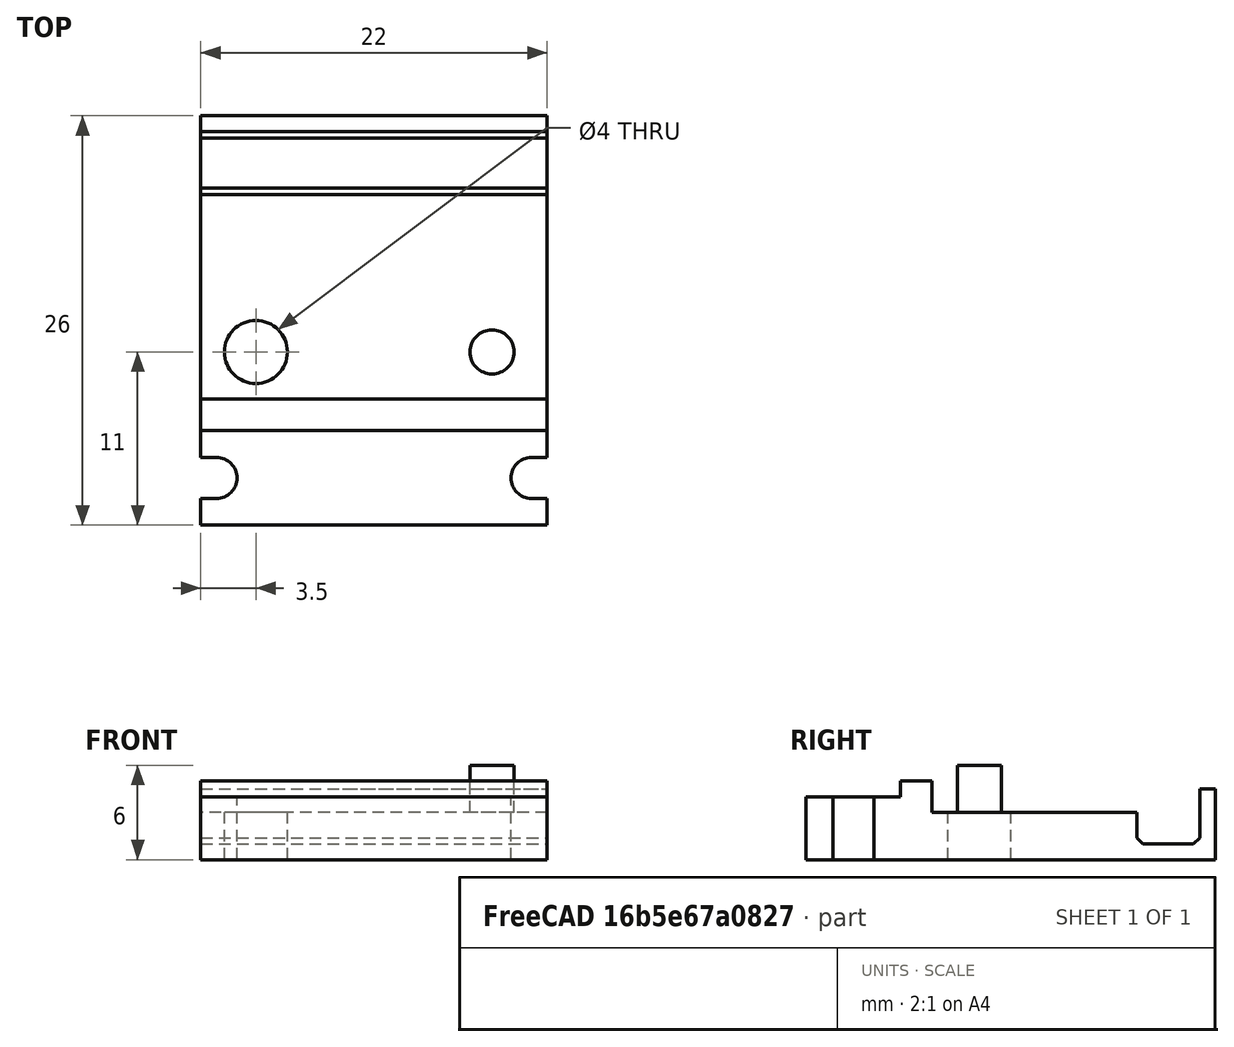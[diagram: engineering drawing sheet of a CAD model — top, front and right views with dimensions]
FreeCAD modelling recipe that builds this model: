
FCSTD DOCUMENT  (FreeCAD 0.18R16146 (Git))
Label: sensor-mount
License: All rights reserved
LicenseURL: http://en.wikipedia.org/wiki/All_rights_reserved
objects: Part::Box×4, Part::MultiFuse×4, Part::Cylinder×3, Part::Cut×3, Part::Feature×1
note: 15 computed .brp shape members not serialized (recipe doc carries the construction recipe); baked Part::Feature solids carry a one-line shape summary decoded from their .brp

FEATURE [Part::Feature] Chamfer002001  label="sensor-r002"
  Placement = pos=(0,0,3) rot=(0,0,1;0rad)
  shape: bbox 22 x 28 x 6 mm, 33 faces (baked)
FEATURE [Part::Cylinder] Cylinder
  Angle = 360
  AttacherType = Attacher::AttachEngine3D
  Height = 10
  Placement = pos=(-10,-5,0) rot=(0,0,1;0rad)
  Radius = 1.3
FEATURE [Part::Cylinder] Cylinder001
  Angle = 360
  AttacherType = Attacher::AttachEngine3D
  Height = 10
  Placement = pos=(10,-5,0) rot=(0,0,1;0rad)
  Radius = 1.3
FEATURE [Part::Box] Box001  label="Cube001"
  AttacherType = Attacher::AttachEngine3D
  Height = 10
  Length = 8
  Placement = pos=(10,-6.3,0) rot=(0,0,1;0rad)
  Width = 2.6
FEATURE [Part::Box] Box002  label="Cube002"
  AttacherType = Attacher::AttachEngine3D
  Height = 10
  Length = 8
  Placement = pos=(-18,-6.3,0) rot=(0,0,1;0rad)
  Width = 2.6
FEATURE [Part::Box] Box003  label="Cube003"
  AttacherType = Attacher::AttachEngine3D
  Height = 10
  Length = 10
  Placement = pos=(-12,18,0) rot=(0,0,1;0rad)
  Width = 10
FEATURE [Part::Cut] Cut
  Base = -> Chamfer002001
  Tool = -> Box003
FEATURE [Part::Box] Box  label="Cube"
  AttacherType = Attacher::AttachEngine3D
  Height = 4
  Length = 22
  Placement = pos=(-11,-8,0) rot=(0,0,1;0rad)
  Width = 6
FEATURE [Part::MultiFuse] Fusion001
  Shapes = -> [Box001,Cylinder001]
FEATURE [Part::MultiFuse] Fusion
  Shapes = -> [Cylinder,Box002]
FEATURE [Part::MultiFuse] Fusion002
  Shapes = -> [Fusion,Fusion001]
FEATURE [Part::Cut] Cut001
  Base = -> Box
  Tool = -> Fusion002
FEATURE [Part::Cylinder] Cylinder002
  Angle = 360
  AttacherType = Attacher::AttachEngine3D
  Height = 3
  Placement = pos=(-7.5,3,0) rot=(0,0,1;0rad)
  Radius = 2
FEATURE [Part::Cut] Cut002
  Base = -> Cut
  Tool = -> Cylinder002
FEATURE [Part::MultiFuse] Fusion003
  Shapes = -> [Cut002,Cut001]
